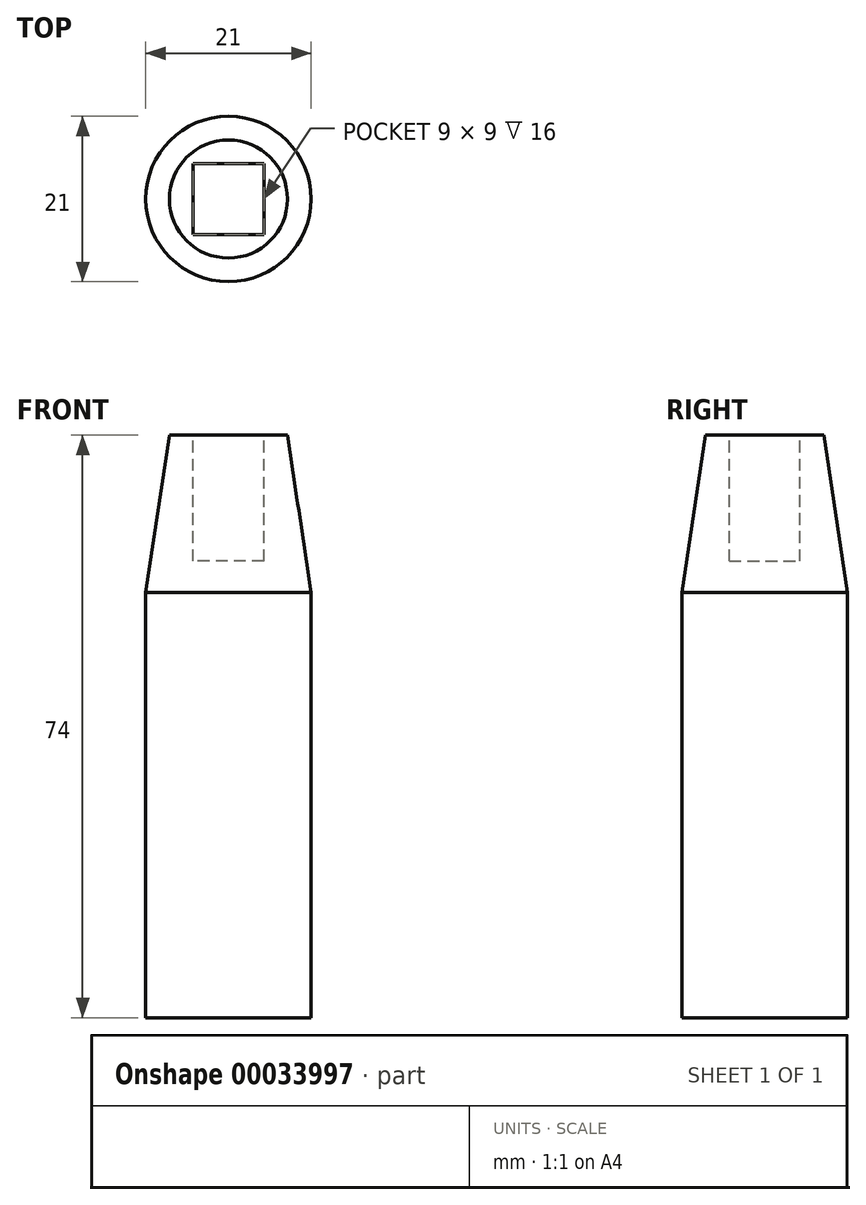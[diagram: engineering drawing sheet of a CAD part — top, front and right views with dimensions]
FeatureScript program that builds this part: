
annotation { "Feature Type Name" : "Feature", "Feature Type Description" : "" }
export const myFeature = defineFeature(function(context is Context, id is Id, definition is map)
    precondition{}
    {
        {
            var Q0;
            Q0=qCreatedBy(makeId("Top.planeOp"),FACE);
            var sketch = newSketch(context, id + "F0", { "sketchPlane" : qUnion([Q0])});
            skCircle(sketch, "E0", {"center": v(0, 0) * mm, "radius": 10.5 * mm});
            skSolve(sketch);
        }
        {
            var Q0;
            Q0 = qSketchRegion(id + "F0", true);
            extrude(context, id + "F1", {"entities" : qUnion([Q0]), "depth" : 54 * mm});
        }
        {
            var Q0;
            Q0=makeQuery(id+"F1.opExtrude","CAP_FACE",FACE,{"disambiguationData":[OSD([sQuery(id+"F0.wireOp",EDGE,"E0")])],"isStart":false});
            cPlane(context, id + "F2", {"entities" : qUnion([Q0]), "cplaneType" : CPlaneType.OFFSET, "offset" : 20 * mm, "width" : 150 * mm, "height" : 150 * mm});
        }
        {
            var Q0;
            Q0=qCreatedBy(id+"F2.planeOp",FACE);
            var sketch = newSketch(context, id + "F3", { "sketchPlane" : qUnion([Q0])});
            skCircle(sketch, "E1", {"center": v(0, 0) * mm, "radius": 7.5 * mm});
            skSolve(sketch);
        }
        {
            var Q1;
            Q1=makeQuery(id+"F3.imprint","IMPRINT",FACE,{"disambiguationData":[TD([[makeQuery(id+"F3.imprint","IMPRINT",EDGE,{"derivedFrom":sQuery(id+"F3.wireOp",EDGE,"E1")}),1.0]])]});
            var Q2;
            Q2=makeQuery(id+"F1.opExtrude","CAP_FACE",FACE,{"disambiguationData":[OSD([sQuery(id+"F0.wireOp",EDGE,"E0")])],"isStart":false});
            loft(context, id + "F4", {"operationType" : NewBodyOperationType.ADD, "sheetProfilesArray" : [{ "sheetProfileEntities" : qUnion([Q1]) }, { "sheetProfileEntities" : qUnion([Q2]) }]});
        }
        {
            var Q0;
            Q0=makeQuery(id+"F4.opLoft","CAP_FACE",FACE,{"disambiguationData":[OSD([makeQuery(id+"F3.imprint","IMPRINT",FACE,{"disambiguationData":[TD([[makeQuery(id+"F3.imprint","IMPRINT",EDGE,{"derivedFrom":sQuery(id+"F3.wireOp",EDGE,"E1")}),1.0]])]})])],"isStart":true});
            var sketch = newSketch(context, id + "F5", { "sketchPlane" : qUnion([Q0])});
            skLineSegment(sketch, "E2.rect.bottom", {"start": v(4.5, -4.5) * mm, "end": v(-4.5, -4.5) * mm});
            skLineSegment(sketch, "E2.rect.top", {"start": v(4.5, 4.5) * mm, "end": v(-4.5, 4.5) * mm});
            skLineSegment(sketch, "E2.rect.left", {"start": v(4.5, -4.5) * mm, "end": v(4.5, 4.5) * mm});
            skLineSegment(sketch, "E2.rect.right", {"start": v(-4.5, -4.5) * mm, "end": v(-4.5, 4.5) * mm});
            skPoint(sketch, "E2.rect.middle", {"position": v(0, 0) * mm});
            skSolve(sketch);
        }
        {
            var Q0;
            Q0 = qSketchRegion(id + "F5", true);
            extrude(context, id + "F6", {"entities" : qUnion([Q0]), "operationType" : NewBodyOperationType.REMOVE, "oppositeDirection" : true, "depth" : 16 * mm});
        }
    });
